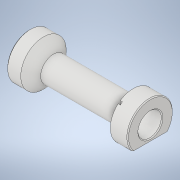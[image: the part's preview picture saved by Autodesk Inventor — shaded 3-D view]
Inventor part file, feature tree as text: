
AUTODESK INVENTOR PART (.ipt)
format: ipt  version: 2020 (Build 240168000, 168)  size: 212,480 bytes
history: native  units: mm
features: sketch x5, projected_geometry x4, chamfer x3, plane x3, extrude x3, revolve x2, fillet x2, mirror x1, pattern_circular x1, hole x1
ambient origin geometry x8: Origin, YZ Plane, XZ Plane, XY Plane, X Axis, Y Axis, Z Axis, Center Point
bodies: Volumenkörper1 (feature_tree)
feature tree (25):
  revolve  "Umdrehung1"
  chamfer  "Fase1"  Distance=2.0mm Angle=45.0deg
  plane  "Arbeitsebene1"
  plane  "Arbeitsebene2"
  extrude  "Extrusion1"  Depth=1.5mm TaperAngle=0.0deg
  mirror  "Spiegeln2"
  fillet  "Rundung1"  Radius=3.0mm
  plane  "Arbeitsebene3"
  extrude  "Extrusion2"  [1 undecoded]
  chamfer  "Fase3"  Distance=2.1mm
  chamfer  "Fase4"  Distance=7.0mm
  revolve  "Umdrehung2"
  pattern_circular  "Runde Anordnung1"  [2 undecoded]
  extrude  "Extrusion3"  Depth=2.0mm TaperAngle=45.0deg
  fillet  "Rundung2"  Radius=0.5mm
  hole  "Bohrung1"  [1 undecoded]
  sketch  "Skizze2"  dims[d6=10.8mm]
  projected_geometry  "Projizierte Kontur1"
  sketch  "Skizze3"  dims[d7=90.0deg]
  projected_geometry  "Projizierte Kontur2"
  projected_geometry  "Projizierte Kontur3"
  projected_geometry  "Projizierte Kontur4"
  sketch  "Skizze4"  dims[d8=21.0mm d9=0.4mm d10=2.0mm d11=45.0deg]
  sketch  "Skizze5"  dims[d12=1.0mm d13=1.5mm d14=0.0mm d15=3.0mm]
  sketch  "Skizze7"  dims[d16=0.1mm d20=-8.6mm d21=2.1mm d22=0.0mm d23=7.0mm d24=3.0mm d25=0.99mm d26=2.0mm d27=45.0deg d28=0.5mm d29=3.99mm d30=2.0mm d31=45.0deg d33=55.8mm d34=8.0mm d35=45.0deg d36=36.8mm d37=3.0mm d38=3.490659mm d39=20.0mm d40=360.0deg d42=1.0mm d43=1.0mm d44=0.0mm d45=2.0mm d46=8.0mm d47=2.2mm d48=6.0mm d49=4.0mm d50=2.0mm d51=90.0deg d52=23.5mm d53=90.0deg d54=2.1mm d55=0.0mm d56=0.5mm d57=0.872665mm]
note: 4 required parameter values undecoded (feature->parameter linkage not recoverable at this tier; creation-order binding heuristic only, values carry confidence <= 0.55)
